# Revit family: Gira_2282005
name_source: partatom
category: Elektroinstallationen
revit_build: Autodesk Revit 2017 (Build: 20160225_1515(x64)
units: mm (PartAtom-declared; Revit-internal decimal feet)

## family parameters
Basisbauteil = Fläche
Beim Laden mit Abzugskörper schneiden = Nein
Bemaßung runder Anschluss = Durchmesser verwenden
Beschriftungsausrichtung beibehalten = Ja
Gemeinsam genutzt = Nein
Raumberechnungspunkt = Nein
Teiletyp = Normal

## types (1)
- UP-Radio RDS Lautsprecher System 55 Schwarz m
    Ausführung = Radio (*en-EN)
    Ausführung der Oberfläche = matt
    Bauelement = Sys55_Komplettgerät_UP-Radio
    Befestigungsart = Krallen-/Schraubbefestigung
    Beschreibung = Unterputz-Radio RDS mit einem Lautsprecher Bedienaufsatz in Schwarzglasoptik Schwarz matt Merkmale: - UKW-Radio mit RDS-Anzeige zur Unterputz-Montage. - Das Unterputz-Radio RDS besteht aus einem Einsatz Radio mit Bedienaufsatz und einem Einsatz Lautsprecher mit Abdeckung. - Der Einsatz Radio ist kompakt in einem Unterputz-Einsatz untergebracht und kann somit in eine einzelne Gerätedose installiert werden. - Der Lautsprecher kann mit dem Einsatz Radio in einer Kombination oder auch abgesetzt in eine Gerätedose installiert werden. An den Einsatz Radio können zwei Lautsprecher angeschlossen werden. - Das Radio erkennt angeschlossene Lautsprecher automatisch und schaltet zwischen Stereo- und Monobetrieb um. - Das Display des Bedienaufsatzes zeigt bei einem entsprechenden RDS-Signal den Sendernamen, die Sendefrequenz und die Uhrzeit an. - Die Bedienung des Radios erfolgt über die kapazitiven Tasten des Bedienaufsatzes. Zur Bedienung ist lediglich eine leichte Berührung der Symbole notwendig. - Das Unterputz-Radio RDS verfügt über zwei Speicherplätze, auf denen je ein Sender einfach per Tastenbetätigung gespeichert und abgerufen werden kann. - Über den Nebenstelleneingang kann das Radio z. B. mit einem Lichtschalter oder einem Automatikschalter zusammen mit der Raumbeleuchtung eingeschaltet werden. - Über den Stereo-AUX-Eingang des Radios können externe Audioquellen, z. B. MP3-Player, in das Radio eingespeist werden. Zum Anschluss der externen Audioquelle wird zusätzlich ein Einsatz Cinch-Audio benötigt, welcher an die AUX-Klemmen des Einsatzes Radio angeschlossen wird. - Der Einsatz Dockingstation wird zur Musikwiedergabe direkt an den Stereo-AUX-Eingang angeschlossen. - Im Sleep-Modus schaltet das Radio 30 Minuten nach dem Einschalten automatisch wieder aus.  Hinweise : - In Kombination mit weiteren elektronischen Geräten unter einer gemeinsamen Abdeckung kann es zu Empfangsbeeinträchtigungen kommen.
    Farbe = schwarz
    GTIN = 4010337038054
    HAN = 2280005
    Halogenfrei = Nein
    HeinzeBIM = https://bimportal.heinze.de
    Hersteller = Gira
    Kategorie = Elektronik-Gerät für Installationsschalterprogramme
    Montageart = unter Putz
    Name = UP-Radio RDS Lautsprecher System 55 Schwarz m
    Oberfläche = sonstige
    Region = DE
    Transparent = Nein
    URL = http://katalog.gira.de
    Verfügbar = Ja
    Vorgabe-Ansicht = 1219 mm
    Werkstoff = sonstige
    Werkstoffgüte = sonstige
    Zusammenstellung = Basiselement

## geometry (parser evidence)
native form markers: Sweep x2
no freeform markers — native parametric forms only
